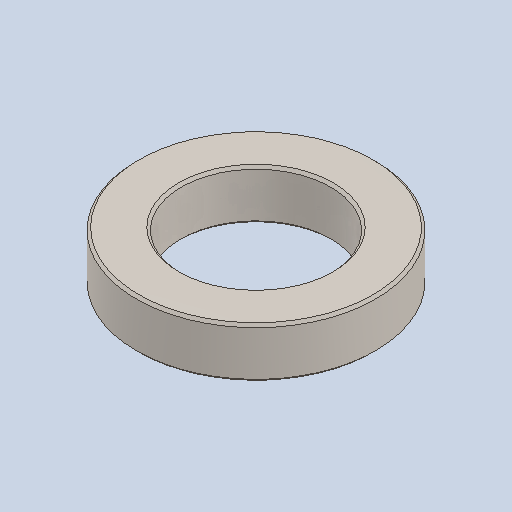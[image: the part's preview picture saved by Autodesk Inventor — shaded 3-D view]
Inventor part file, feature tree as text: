
AUTODESK INVENTOR PART (.ipt)
format: ipt  version: 2023.2 (Build 272271000, 271)  size: 103,424 bytes
history: native  units: in
note: dims shown in document units (in); Inventor stores cm internally (conversion verified against a paired STEP export)
features: chamfer x1
ambient origin geometry x8: Origin, YZ Plane, XZ Plane, XY Plane, X Axis, Y Axis, Z Axis, Center Point
bodies: Solid1 (feature_tree)
feature tree (1):
  chamfer  "Chamfer1"  [1 undecoded]
note: 1 required parameter value undecoded (feature->parameter linkage not recoverable at this tier; creation-order binding heuristic only, values carry confidence <= 0.55)
